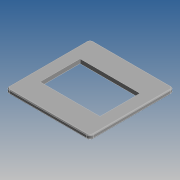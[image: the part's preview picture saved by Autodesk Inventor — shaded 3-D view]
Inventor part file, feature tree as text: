
AUTODESK INVENTOR PART (.ipt)
format: ipt  version: 2015 SP1 (Build 190203100, 203)  size: 215,552 bytes
history: native  units: mm
features: fillet x2, extrude x1, sketch x1
ambient origin geometry x8: Origin, YZ Plane, XZ Plane, XY Plane, X Axis, Y Axis, Z Axis, Center Point
bodies: Solid1 (feature_tree)
feature tree (4):
  extrude  "Extrusion1"  Depth=50.5mm
  fillet  "Fillet1"  Radius=36.0mm
  fillet  "Fillet2"  Radius=24.0mm
  sketch  "Sketch1"  dims[d0=50.5mm d1=50.5mm d2=36.0mm d3=24.0mm d4=2.5mm d5=0.0mm d6=2.0mm d7=0.5mm]
